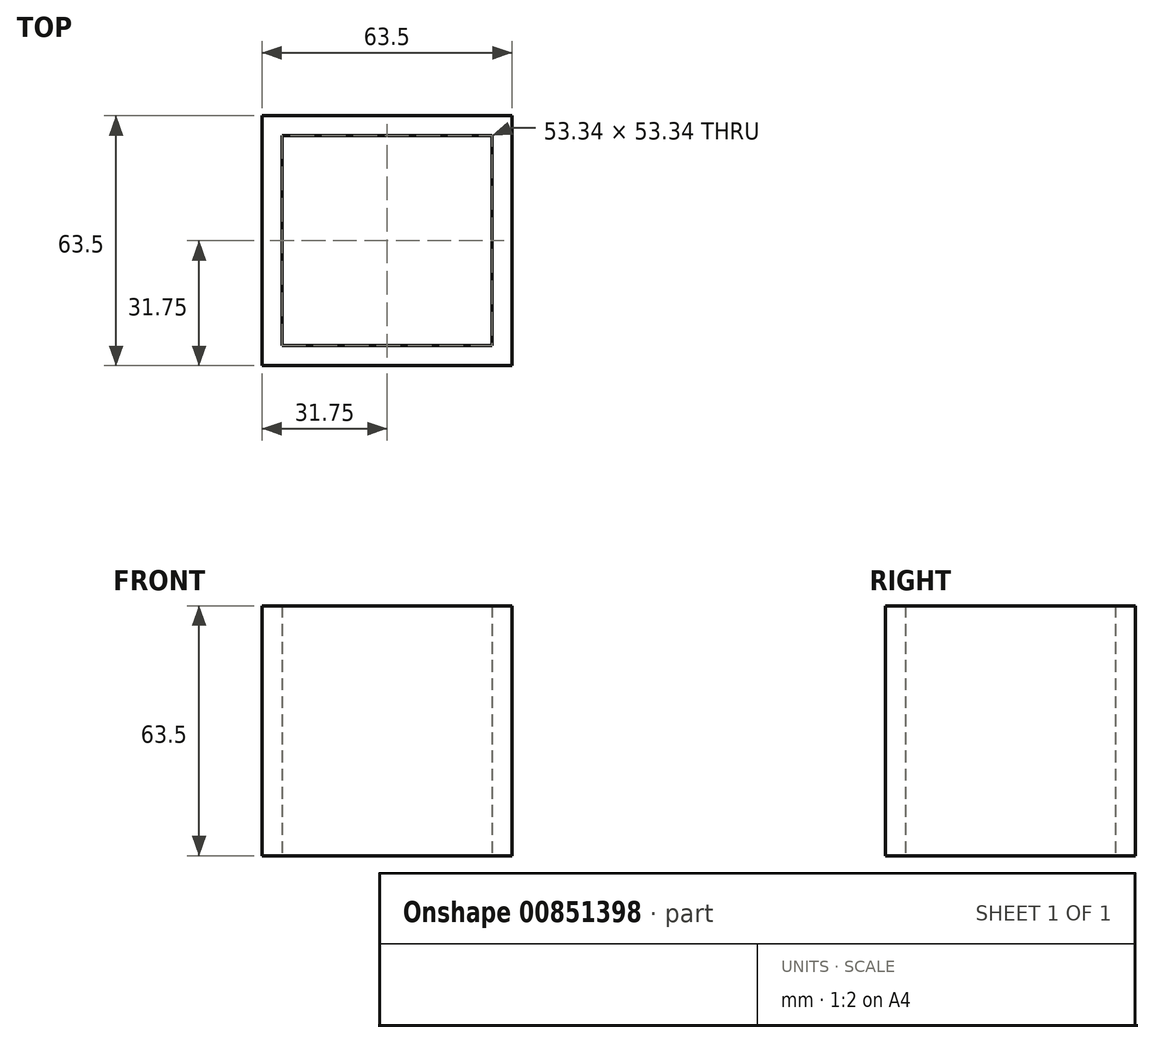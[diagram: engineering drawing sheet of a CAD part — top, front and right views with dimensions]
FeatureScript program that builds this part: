
annotation { "Feature Type Name" : "Feature", "Feature Type Description" : "" }
export const myFeature = defineFeature(function(context is Context, id is Id, definition is map)
    precondition{}
    {
        {
            var Q0;
            Q0=qCreatedBy(makeId("Top.planeOp"),FACE);
            var sketch = newSketch(context, id + "F0", { "sketchPlane" : qUnion([Q0])});
            skLineSegment(sketch, "E0.bottom", {"start": v(-63.5, 63.5) * mm, "end": v(0, 63.5) * mm});
            skLineSegment(sketch, "E0.top", {"start": v(-63.5, 0) * mm, "end": v(0, 0) * mm});
            skLineSegment(sketch, "E0.left", {"start": v(-63.5, 63.5) * mm, "end": v(-63.5, 0) * mm});
            skLineSegment(sketch, "E0.right", {"start": v(0, 63.5) * mm, "end": v(0, 0) * mm});
            skLineSegment(sketch, "E1.bottom", {"start": v(-58.42, 58.42) * mm, "end": v(-5.08, 58.42) * mm});
            skLineSegment(sketch, "E1.top", {"start": v(-58.42, 5.08) * mm, "end": v(-5.08, 5.08) * mm});
            skLineSegment(sketch, "E1.left", {"start": v(-58.42, 58.42) * mm, "end": v(-58.42, 5.08) * mm});
            skLineSegment(sketch, "E1.right", {"start": v(-5.08, 58.42) * mm, "end": v(-5.08, 5.08) * mm});
            skSolve(sketch);
        }
        {
            var Q0;
            Q0 = qSketchRegion(id + "F0", true);
            extrude(context, id + "F1", {"entities" : qUnion([Q0]), "depth" : 63.5 * mm, "offsetDistance" : 25.4 * mm});
        }
    });
